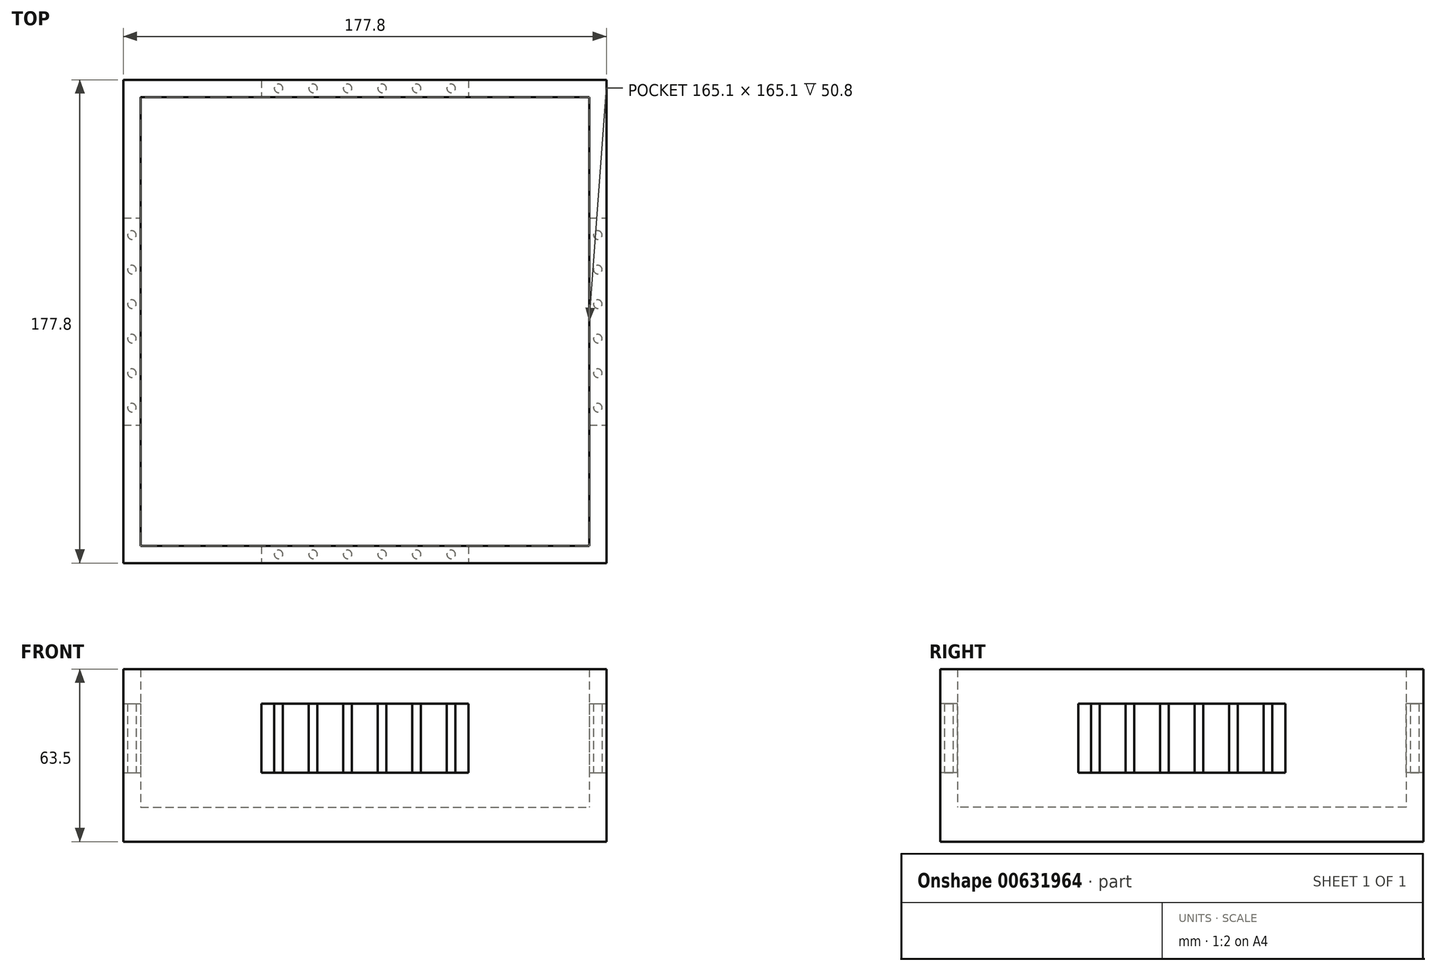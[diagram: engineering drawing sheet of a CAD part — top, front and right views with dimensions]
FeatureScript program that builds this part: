
annotation { "Feature Type Name" : "Feature", "Feature Type Description" : "" }
export const myFeature = defineFeature(function(context is Context, id is Id, definition is map)
    precondition{}
    {
        {
            var Q0;
            Q0=qCreatedBy(makeId("Top.planeOp"),FACE);
            var sketch = newSketch(context, id + "F0", { "sketchPlane" : qUnion([Q0])});
            skLineSegment(sketch, "E0.bottom", {"start": v(0, 177.8) * mm, "end": v(177.8, 177.8) * mm});
            skLineSegment(sketch, "E0.top", {"start": v(0, 0) * mm, "end": v(177.8, 0) * mm});
            skLineSegment(sketch, "E0.left", {"start": v(0, 177.8) * mm, "end": v(0, 0) * mm});
            skLineSegment(sketch, "E0.right", {"start": v(177.8, 177.8) * mm, "end": v(177.8, 0) * mm});
            skSolve(sketch);
        }
        {
            var Q0;
            Q0 = qSketchRegion(id + "F0", true);
            extrude(context, id + "F1", {"entities" : qUnion([Q0]), "depth" : 12.7 * mm, "offsetDistance" : 25.4 * mm});
        }
        {
            var Q0;
            Q0=makeQuery(id+"F1.opExtrude","CAP_FACE",FACE,{"disambiguationData":[OSD([sQuery(id+"F0.wireOp",EDGE,"E0.bottom"),sQuery(id+"F0.wireOp",EDGE,"E0.top"),sQuery(id+"F0.wireOp",EDGE,"E0.left"),sQuery(id+"F0.wireOp",EDGE,"E0.right")])],"isStart":false});
            var sketch = newSketch(context, id + "F2", { "sketchPlane" : qUnion([Q0])});
            skLineSegment(sketch, "E1.bottom", {"start": v(0, 177.8) * mm, "end": v(177.8, 177.8) * mm});
            skLineSegment(sketch, "E1.top", {"start": v(0, 0) * mm, "end": v(177.8, 0) * mm});
            skLineSegment(sketch, "E1.left", {"start": v(0, 177.8) * mm, "end": v(0, 0) * mm});
            skLineSegment(sketch, "E1.right", {"start": v(177.8, 177.8) * mm, "end": v(177.8, 0) * mm});
            skLineSegment(sketch, "E2.bottom", {"start": v(6.35, 171.45) * mm, "end": v(171.45, 171.45) * mm});
            skLineSegment(sketch, "E2.top", {"start": v(6.35, 6.35) * mm, "end": v(171.45, 6.35) * mm});
            skLineSegment(sketch, "E2.left", {"start": v(6.35, 171.45) * mm, "end": v(6.35, 6.35) * mm});
            skLineSegment(sketch, "E2.right", {"start": v(171.45, 171.45) * mm, "end": v(171.45, 6.35) * mm});
            skLineSegment(sketch, "E3", {"start": v(6.35, 171.45) * mm, "end": v(171.45, 6.35) * mm, "construction": true});
            skLineSegment(sketch, "E4", {"start": v(177.8, 177.8) * mm, "end": v(0, 0) * mm, "construction": true});
            skPoint(sketch, "E5", {"position": v(88.9, 88.9) * mm});
            skSolve(sketch);
        }
        {
            var Q0;
            Q0 = qSketchRegion(id + "F2", true);
            extrude(context, id + "F3", {"entities" : qUnion([Q0]), "operationType" : NewBodyOperationType.ADD, "depth" : 50.8 * mm, "offsetDistance" : 25.4 * mm});
        }
        {
            var Q0;
            Q0=makeQuery(id+"F3.boolean.opBoolean","MERGE",FACE,{"derivedFrom":[makeQuery(id+"F1.opExtrude","SWEPT_FACE",FACE,{"disambiguationData":[OSD([sQuery(id+"F0.wireOp",EDGE,"E0.right")])]}),makeQuery(id+"F3.opExtrude","SWEPT_FACE",FACE,{"disambiguationData":[OSD([sQuery(id+"F2.wireOp",EDGE,"E1.right")])]})]});
            var sketch = newSketch(context, id + "F4", { "sketchPlane" : qUnion([Q0])});
            skLineSegment(sketch, "E6.bottom", {"start": v(50.8, 50.8) * mm, "end": v(127, 50.8) * mm});
            skLineSegment(sketch, "E6.top", {"start": v(50.8, 25.4) * mm, "end": v(127, 25.4) * mm});
            skLineSegment(sketch, "E6.left", {"start": v(50.8, 50.8) * mm, "end": v(50.8, 25.4) * mm});
            skLineSegment(sketch, "E6.right", {"start": v(127, 50.8) * mm, "end": v(127, 25.4) * mm});
            skLineSegment(sketch, "E7", {"start": v(88.9, 63.5) * mm, "end": v(88.9, 12.7) * mm, "construction": true});
            skLineSegment(sketch, "E8", {"start": v(50.8, 25.4) * mm, "end": v(127, 50.8) * mm, "construction": true});
            skPoint(sketch, "E9", {"position": v(88.9, 38.1) * mm});
            skSolve(sketch);
        }
        {
            var Q0;
            Q0 = qSketchRegion(id + "F4", true);
            var Q1;
            Q1=makeQuery(id+"F3.boolean.opBoolean","MERGE",FACE,{"derivedFrom":[makeQuery(id+"F1.opExtrude","SWEPT_FACE",FACE,{"disambiguationData":[OSD([sQuery(id+"F0.wireOp",EDGE,"E0.left")])]}),makeQuery(id+"F3.opExtrude","SWEPT_FACE",FACE,{"disambiguationData":[OSD([sQuery(id+"F2.wireOp",EDGE,"E1.left")])]})]});
            extrude(context, id + "F5", {"entities" : qUnion([Q0]), "operationType" : NewBodyOperationType.REMOVE, "endBound" : BoundingType.UP_TO_SURFACE, "oppositeDirection" : true, "depth" : 25.4 * mm, "endBoundEntityFace" : qUnion([Q1]), "offsetDistance" : 25.4 * mm});
        }
        {
            var Q0;
            Q0=makeQuery(id+"F3.boolean.opBoolean","MERGE",FACE,{"derivedFrom":[makeQuery(id+"F1.opExtrude","SWEPT_FACE",FACE,{"disambiguationData":[OSD([sQuery(id+"F0.wireOp",EDGE,"E0.top")])]}),makeQuery(id+"F3.opExtrude","SWEPT_FACE",FACE,{"disambiguationData":[OSD([sQuery(id+"F2.wireOp",EDGE,"E1.top")])]})]});
            var sketch = newSketch(context, id + "F6", { "sketchPlane" : qUnion([Q0])});
            skLineSegment(sketch, "E10.bottom", {"start": v(50.8, 50.8) * mm, "end": v(127, 50.8) * mm});
            skLineSegment(sketch, "E10.top", {"start": v(50.8, 25.4) * mm, "end": v(127, 25.4) * mm});
            skLineSegment(sketch, "E10.left", {"start": v(50.8, 50.8) * mm, "end": v(50.8, 25.4) * mm});
            skLineSegment(sketch, "E10.right", {"start": v(127, 50.8) * mm, "end": v(127, 25.4) * mm});
            skLineSegment(sketch, "E11", {"start": v(127, 50.8) * mm, "end": v(50.8, 25.4) * mm, "construction": true});
            skLineSegment(sketch, "E12", {"start": v(88.9, 63.5) * mm, "end": v(88.9, 12.7) * mm, "construction": true});
            skPoint(sketch, "E13", {"position": v(88.9, 38.1) * mm});
            skSolve(sketch);
        }
        {
            var Q0;
            Q0 = qSketchRegion(id + "F6", true);
            var Q1;
            Q1=makeQuery(id+"F3.boolean.opBoolean","MERGE",FACE,{"derivedFrom":[makeQuery(id+"F1.opExtrude","SWEPT_FACE",FACE,{"disambiguationData":[OSD([sQuery(id+"F0.wireOp",EDGE,"E0.bottom")])]}),makeQuery(id+"F3.opExtrude","SWEPT_FACE",FACE,{"disambiguationData":[OSD([sQuery(id+"F2.wireOp",EDGE,"E1.bottom")])]})]});
            extrude(context, id + "F7", {"entities" : qUnion([Q0]), "operationType" : NewBodyOperationType.REMOVE, "endBound" : BoundingType.UP_TO_SURFACE, "oppositeDirection" : true, "depth" : 25.4 * mm, "endBoundEntityFace" : qUnion([Q1]), "offsetDistance" : 25.4 * mm});
        }
        {
            var Q0;
            Q0=makeQuery(id+"F5.boolean.opBoolean","COPY",FACE,{"disambiguationData":[TD([makeQuery(id+"F1.opExtrude","SWEPT_FACE",FACE,{"disambiguationData":[OSD([sQuery(id+"F0.wireOp",EDGE,"E0.right")])]})])],"derivedFrom":makeQuery(id+"F5.opExtrude","SWEPT_FACE",FACE,{"disambiguationData":[OSD([sQuery(id+"F4.wireOp",EDGE,"E6.top")])]})});
            var sketch = newSketch(context, id + "F8", { "sketchPlane" : qUnion([Q0])});
            skLineSegment(sketch, "E14", {"start": v(174.62, 50.8) * mm, "end": v(174.62, 63.5) * mm, "construction": true});
            skLineSegment(sketch, "E15", {"start": v(174.62, 63.5) * mm, "end": v(174.62, 76.2) * mm, "construction": true});
            skLineSegment(sketch, "E16", {"start": v(174.62, 76.2) * mm, "end": v(174.62, 88.9) * mm, "construction": true});
            skLineSegment(sketch, "E17", {"start": v(174.62, 88.9) * mm, "end": v(174.62, 101.6) * mm, "construction": true});
            skLineSegment(sketch, "E18", {"start": v(174.62, 101.6) * mm, "end": v(174.62, 114.3) * mm, "construction": true});
            skLineSegment(sketch, "E19", {"start": v(174.62, 114.3) * mm, "end": v(174.62, 127) * mm, "construction": true});
            skCircle(sketch, "E20", {"center": v(174.62, 69.85) * mm, "radius": 1.59 * mm});
            skCircle(sketch, "E21", {"center": v(174.62, 57.15) * mm, "radius": 1.59 * mm});
            skCircle(sketch, "E22", {"center": v(174.62, 82.55) * mm, "radius": 1.59 * mm});
            skCircle(sketch, "E23", {"center": v(174.62, 107.95) * mm, "radius": 1.59 * mm});
            skCircle(sketch, "E24", {"center": v(174.62, 120.65) * mm, "radius": 1.59 * mm});
            skCircle(sketch, "E25", {"center": v(174.62, 95.25) * mm, "radius": 1.59 * mm});
            skLineSegment(sketch, "E26", {"start": v(50.8, 174.63) * mm, "end": v(63.5, 174.63) * mm, "construction": true});
            skLineSegment(sketch, "E27", {"start": v(63.5, 174.63) * mm, "end": v(76.2, 174.63) * mm, "construction": true});
            skLineSegment(sketch, "E28", {"start": v(76.2, 174.63) * mm, "end": v(88.9, 174.63) * mm, "construction": true});
            skLineSegment(sketch, "E29", {"start": v(88.9, 174.63) * mm, "end": v(101.6, 174.63) * mm, "construction": true});
            skLineSegment(sketch, "E30", {"start": v(101.6, 174.63) * mm, "end": v(114.3, 174.63) * mm, "construction": true});
            skLineSegment(sketch, "E31", {"start": v(114.3, 174.63) * mm, "end": v(127, 174.63) * mm, "construction": true});
            skCircle(sketch, "E32", {"center": v(69.85, 174.63) * mm, "radius": 1.59 * mm});
            skCircle(sketch, "E33", {"center": v(57.15, 174.63) * mm, "radius": 1.59 * mm});
            skCircle(sketch, "E34", {"center": v(82.55, 174.63) * mm, "radius": 1.59 * mm});
            skCircle(sketch, "E35", {"center": v(107.95, 174.63) * mm, "radius": 1.59 * mm});
            skCircle(sketch, "E36", {"center": v(120.65, 174.63) * mm, "radius": 1.59 * mm});
            skCircle(sketch, "E37", {"center": v(95.25, 174.63) * mm, "radius": 1.59 * mm});
            skLineSegment(sketch, "E38", {"start": v(50.8, 3.18) * mm, "end": v(63.5, 3.18) * mm, "construction": true});
            skLineSegment(sketch, "E39", {"start": v(63.5, 3.18) * mm, "end": v(76.2, 3.18) * mm, "construction": true});
            skLineSegment(sketch, "E40", {"start": v(76.2, 3.18) * mm, "end": v(88.9, 3.18) * mm, "construction": true});
            skLineSegment(sketch, "E41", {"start": v(88.9, 3.18) * mm, "end": v(101.6, 3.18) * mm, "construction": true});
            skLineSegment(sketch, "E42", {"start": v(101.6, 3.18) * mm, "end": v(114.3, 3.18) * mm, "construction": true});
            skLineSegment(sketch, "E43", {"start": v(114.3, 3.18) * mm, "end": v(127, 3.18) * mm, "construction": true});
            skCircle(sketch, "E44", {"center": v(69.85, 3.18) * mm, "radius": 1.59 * mm});
            skCircle(sketch, "E45", {"center": v(57.15, 3.18) * mm, "radius": 1.59 * mm});
            skCircle(sketch, "E46", {"center": v(82.55, 3.18) * mm, "radius": 1.59 * mm});
            skCircle(sketch, "E47", {"center": v(107.95, 3.18) * mm, "radius": 1.59 * mm});
            skCircle(sketch, "E48", {"center": v(120.65, 3.18) * mm, "radius": 1.59 * mm});
            skCircle(sketch, "E49", {"center": v(95.25, 3.18) * mm, "radius": 1.59 * mm});
            skLineSegment(sketch, "E50", {"start": v(3.17, 50.8) * mm, "end": v(3.17, 63.5) * mm, "construction": true});
            skLineSegment(sketch, "E51", {"start": v(3.17, 63.5) * mm, "end": v(3.17, 76.2) * mm, "construction": true});
            skLineSegment(sketch, "E52", {"start": v(3.17, 76.2) * mm, "end": v(3.17, 88.9) * mm, "construction": true});
            skLineSegment(sketch, "E53", {"start": v(3.17, 88.9) * mm, "end": v(3.17, 101.6) * mm, "construction": true});
            skLineSegment(sketch, "E54", {"start": v(3.17, 101.6) * mm, "end": v(3.17, 114.3) * mm, "construction": true});
            skLineSegment(sketch, "E55", {"start": v(3.17, 114.3) * mm, "end": v(3.17, 127) * mm, "construction": true});
            skCircle(sketch, "E56", {"center": v(3.17, 69.85) * mm, "radius": 1.59 * mm});
            skCircle(sketch, "E57", {"center": v(3.17, 57.15) * mm, "radius": 1.59 * mm});
            skCircle(sketch, "E58", {"center": v(3.17, 82.55) * mm, "radius": 1.59 * mm});
            skCircle(sketch, "E59", {"center": v(3.17, 107.95) * mm, "radius": 1.59 * mm});
            skCircle(sketch, "E60", {"center": v(3.17, 120.65) * mm, "radius": 1.59 * mm});
            skCircle(sketch, "E61", {"center": v(3.17, 95.25) * mm, "radius": 1.59 * mm});
            skSolve(sketch);
        }
        {
            var Q0;
            Q0 = qSketchRegion(id + "F8", true);
            var Q1;
            Q1=makeQuery(id+"F5.boolean.opBoolean","COPY",FACE,{"disambiguationData":[TD([makeQuery(id+"F1.opExtrude","SWEPT_FACE",FACE,{"disambiguationData":[OSD([sQuery(id+"F0.wireOp",EDGE,"E0.right")])]})])],"derivedFrom":makeQuery(id+"F5.opExtrude","SWEPT_FACE",FACE,{"disambiguationData":[OSD([sQuery(id+"F4.wireOp",EDGE,"E6.bottom")])]})});
            extrude(context, id + "F9", {"entities" : qUnion([Q0]), "operationType" : NewBodyOperationType.ADD, "endBound" : BoundingType.UP_TO_SURFACE, "depth" : 25.4 * mm, "endBoundEntityFace" : qUnion([Q1]), "offsetDistance" : 25.4 * mm});
        }
    });
